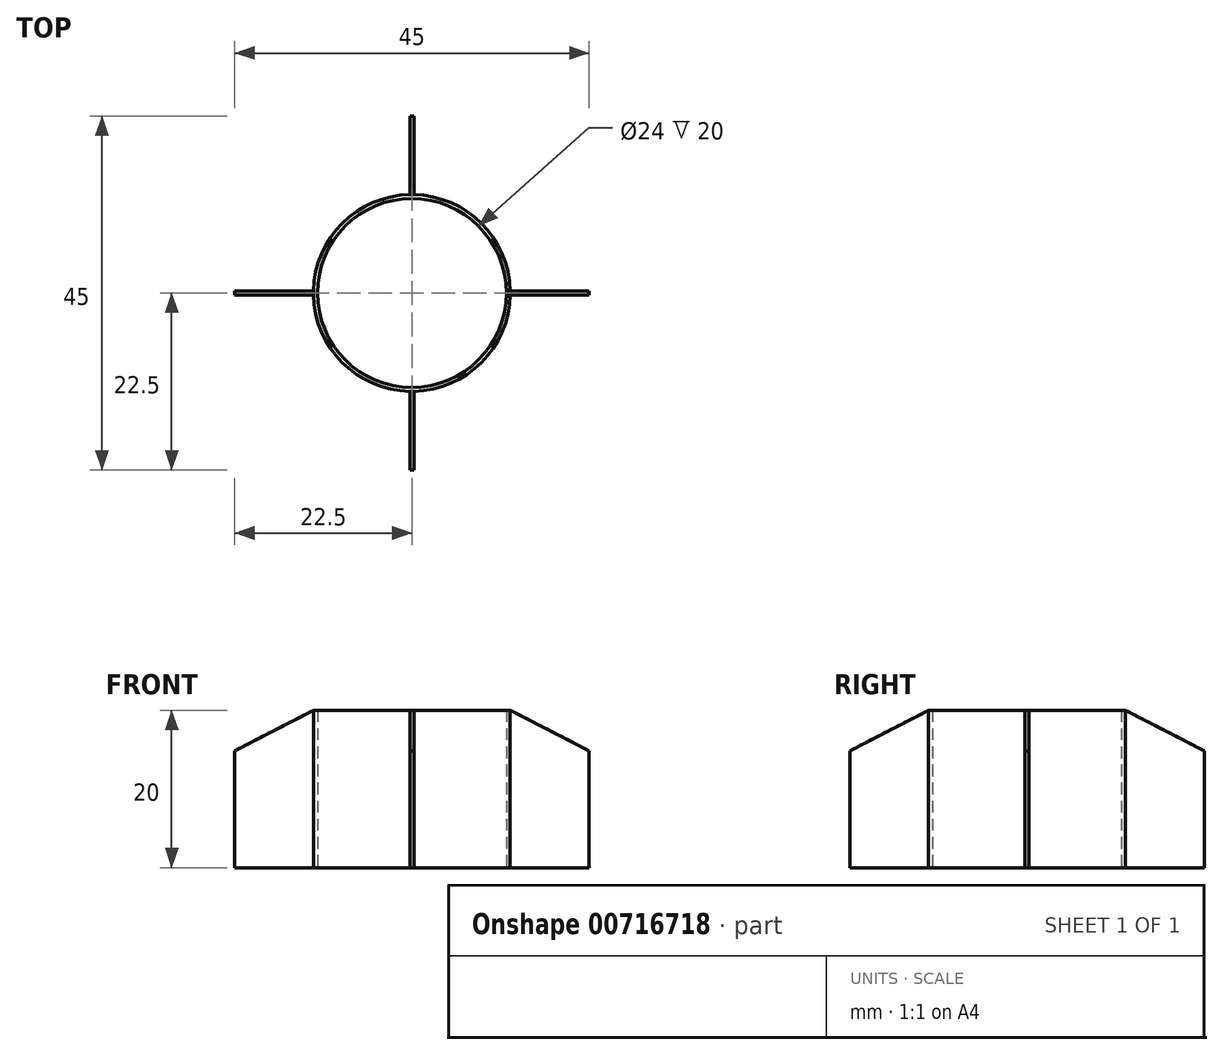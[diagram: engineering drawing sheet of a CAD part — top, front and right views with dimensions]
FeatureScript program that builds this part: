
annotation { "Feature Type Name" : "Feature", "Feature Type Description" : "" }
export const myFeature = defineFeature(function(context is Context, id is Id, definition is map)
    precondition{}
    {
        {
            var Q0;
            Q0=qCreatedBy(makeId("Top.planeOp"),FACE);
            var sketch = newSketch(context, id + "F0", { "sketchPlane" : qUnion([Q0])});
            skCircle(sketch, "E0", {"center": v(0, 0) * mm, "radius": 12.5 * mm});
            skCircle(sketch, "E1", {"center": v(0, 0) * mm, "radius": 12 * mm});
            skLineSegment(sketch, "E2.bottom", {"start": v(0.25, 12.5) * mm, "end": v(-0.25, 12.5) * mm});
            skLineSegment(sketch, "E2.top", {"start": v(0.25, 22.5) * mm, "end": v(-0.25, 22.5) * mm});
            skLineSegment(sketch, "E2.left", {"start": v(0.25, 12.5) * mm, "end": v(0.25, 22.5) * mm});
            skLineSegment(sketch, "E2.right", {"start": v(-0.25, 12.5) * mm, "end": v(-0.25, 22.5) * mm});
            skPoint(sketch, "E2.middle", {"position": v(0, 17.5) * mm});
            skLineSegment(sketch, "E3.left", {"start": v(-12.5, 0) * mm, "end": v(-12.5, 0) * mm});
            skLineSegment(sketch, "E3.right", {"start": v(-22.5, 0) * mm, "end": v(-22.5, 0) * mm});
            skPoint(sketch, "E3.middle", {"position": v(-17.5, 0) * mm});
            skLineSegment(sketch, "E4.bottom", {"start": v(-12.5, 0.25) * mm, "end": v(-22.5, 0.25) * mm});
            skLineSegment(sketch, "E4.top", {"start": v(-12.5, -0.25) * mm, "end": v(-22.5, -0.25) * mm});
            skLineSegment(sketch, "E4.left", {"start": v(-12.5, 0.25) * mm, "end": v(-12.5, -0.25) * mm});
            skLineSegment(sketch, "E4.right", {"start": v(-22.5, 0.25) * mm, "end": v(-22.5, -0.25) * mm});
            skLineSegment(sketch, "E5.bottom", {"start": v(0.25, -12.5) * mm, "end": v(-0.25, -12.5) * mm});
            skLineSegment(sketch, "E5.top", {"start": v(0.25, -22.5) * mm, "end": v(-0.25, -22.5) * mm});
            skLineSegment(sketch, "E5.left", {"start": v(0.25, -12.5) * mm, "end": v(0.25, -22.5) * mm});
            skLineSegment(sketch, "E5.right", {"start": v(-0.25, -12.5) * mm, "end": v(-0.25, -22.5) * mm});
            skPoint(sketch, "E5.middle", {"position": v(0, -17.5) * mm});
            skLineSegment(sketch, "E6.bottom", {"start": v(12.5, 0.25) * mm, "end": v(22.5, 0.25) * mm});
            skLineSegment(sketch, "E6.top", {"start": v(12.5, -0.25) * mm, "end": v(22.5, -0.25) * mm});
            skLineSegment(sketch, "E6.left", {"start": v(12.5, 0.25) * mm, "end": v(12.5, -0.25) * mm});
            skLineSegment(sketch, "E6.right", {"start": v(22.5, 0.25) * mm, "end": v(22.5, -0.25) * mm});
            skPoint(sketch, "E6.middle", {"position": v(17.5, 0) * mm});
            skSolve(sketch);
        }
        {
            var Q0;
            Q0 = qSketchRegion(id + "F0", true);
            extrude(context, id + "F1", {"entities" : qUnion([Q0]), "depth" : 20 * mm, "offsetDistance" : 25 * mm});
        }
        {
            var Q0;
            Q0=makeQuery(id+"F1.opExtrude","SWEPT_FACE",FACE,{"disambiguationData":[OSD([sQuery(id+"F0.wireOp",EDGE,"E5.left")])]});
            var sketch = newSketch(context, id + "F2", { "sketchPlane" : qUnion([Q0])});
            skLineSegment(sketch, "E7", {"start": v(-12.5, 20) * mm, "end": v(-22.5, 14.85) * mm});
            skLineSegment(sketch, "E8", {"start": v(-22.5, 14.85) * mm, "end": v(-22.5, 5.6) * mm});
            skLineSegment(sketch, "E9", {"start": v(-22.5, 5.6) * mm, "end": v(-12.5, 0) * mm});
            skLineSegment(sketch, "E10", {"start": v(-12.5, 0) * mm, "end": v(-12.5, 20) * mm});
            skSolve(sketch);
        }
        {
            var Q0;
            {var subQ0=sQuery(id+"F2.wireOp",EDGE,"E7");Q0=makeQuery(id+"F2.imprint","IMPRINT",FACE,{"disambiguationData":[TD([[makeQuery(id+"F2.imprint","IMPRINT",EDGE,{"derivedFrom":subQ0}),-1.0]])]});}
            var Q1;
            Q1=makeQuery(id+"F1.opExtrude","CAP_EDGE",EDGE,{"disambiguationData":[OSD([sQuery(id+"F0.wireOp",EDGE,"E1")])],"isStart":false});
            revolve(context, id + "F3", {"operationType" : NewBodyOperationType.REMOVE, "surfaceOperationType" : NewSurfaceOperationType.NEW, "entities" : qUnion([Q0]), "axis" : qUnion([Q1]), "revolveType" : RevolveType.FULL, "oppositeDirection" : true});
        }
    });
